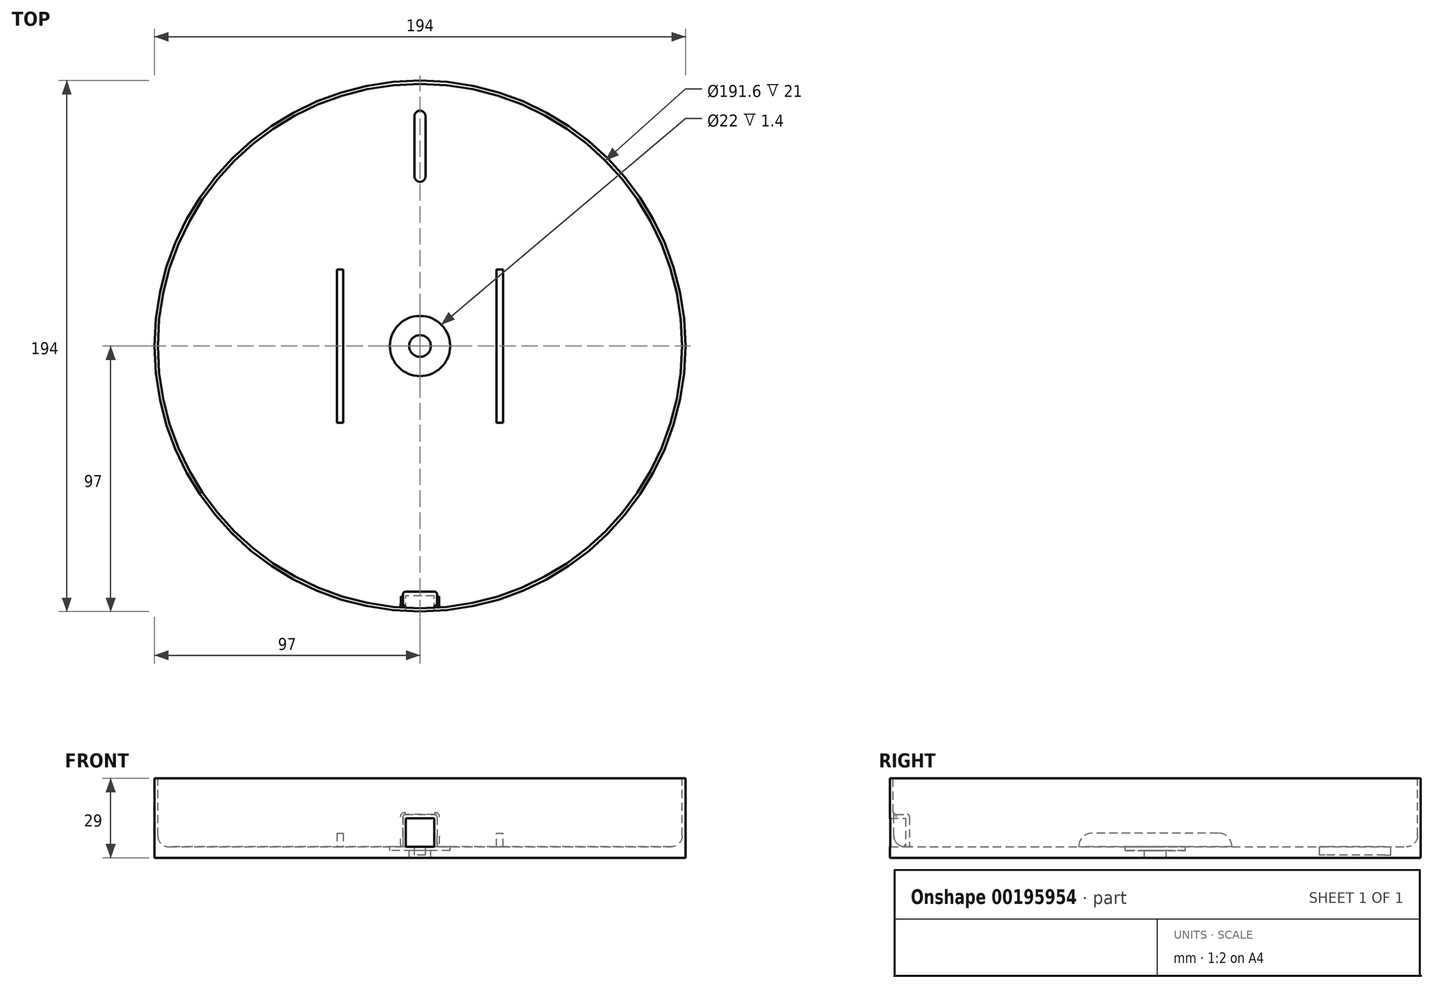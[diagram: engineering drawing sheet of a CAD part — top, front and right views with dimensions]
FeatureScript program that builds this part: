
annotation { "Feature Type Name" : "Feature", "Feature Type Description" : "" }
export const myFeature = defineFeature(function(context is Context, id is Id, definition is map)
    precondition{}
    {
        {
            var Q0;
            Q0=qCreatedBy(makeId("Top.planeOp"),FACE);
            var sketch = newSketch(context, id + "F0", { "sketchPlane" : qUnion([Q0])});
            skCircle(sketch, "E0", {"center": v(0, 0) * mm, "radius": 97 * mm});
            skSolve(sketch);
        }
        {
            var Q0;
            Q0 = qSketchRegion(id + "F0", true);
            extrude(context, id + "F1", {"entities" : qUnion([Q0]), "depth" : 29 * mm});
        }
        {
            var Q0;
            Q0=makeQuery(id+"F1.opExtrude","CAP_FACE",FACE,{"disambiguationData":[OSD([sQuery(id+"F0.wireOp",EDGE,"E0")])],"isStart":false});
            var sketch = newSketch(context, id + "F2", { "sketchPlane" : qUnion([Q0])});
            skCircle(sketch, "E1", {"center": v(0, 0) * mm, "radius": 95.8 * mm});
            skSolve(sketch);
        }
        {
            var Q0;
            Q0 = qSketchRegion(id + "F2", true);
            extrude(context, id + "F3", {"entities" : qUnion([Q0]), "operationType" : NewBodyOperationType.REMOVE, "oppositeDirection" : true, "depth" : 25 * mm});
        }
        {
            var Q0;
            Q0=makeQuery(id+"F3.boolean.opBoolean","COPY",FACE,{"derivedFrom":makeQuery(id+"F3.opExtrude","CAP_FACE",FACE,{"disambiguationData":[OSD([sQuery(id+"F2.wireOp",EDGE,"E1")])],"isStart":false})});
            var sketch = newSketch(context, id + "F4", { "sketchPlane" : qUnion([Q0])});
            skCircle(sketch, "E2", {"center": v(0, 0) * mm, "radius": 3.95 * mm});
            skSolve(sketch);
        }
        {
            var Q0;
            Q0 = qSketchRegion(id + "F4", true);
            extrude(context, id + "F5", {"entities" : qUnion([Q0]), "operationType" : NewBodyOperationType.REMOVE, "oppositeDirection" : true, "depth" : 25 * mm});
        }
        {
            var Q0;
            Q0=makeQuery(id+"F3.boolean.opBoolean","COPY",FACE,{"derivedFrom":makeQuery(id+"F3.opExtrude","CAP_FACE",FACE,{"disambiguationData":[OSD([sQuery(id+"F2.wireOp",EDGE,"E1")])],"isStart":false})});
            var sketch = newSketch(context, id + "F6", { "sketchPlane" : qUnion([Q0])});
            skCircle(sketch, "E3", {"center": v(0, 0) * mm, "radius": 11 * mm});
            skSolve(sketch);
        }
        {
            var Q0;
            Q0 = qSketchRegion(id + "F6", true);
            extrude(context, id + "F7", {"entities" : qUnion([Q0]), "operationType" : NewBodyOperationType.REMOVE, "oppositeDirection" : true, "depth" : 1.4 * mm});
        }
        {
            var Q0;
            Q0=makeQuery(id+"F3.boolean.opBoolean","COPY",FACE,{"derivedFrom":makeQuery(id+"F3.opExtrude","CAP_FACE",FACE,{"disambiguationData":[OSD([sQuery(id+"F2.wireOp",EDGE,"E1")])],"isStart":false})});
            var sketch = newSketch(context, id + "F8", { "sketchPlane" : qUnion([Q0])});
            skLineSegment(sketch, "E4.bottom", {"start": v(-30.4, 28) * mm, "end": v(30.4, 28) * mm});
            skLineSegment(sketch, "E4.top", {"start": v(-30.4, -28) * mm, "end": v(30.4, -28) * mm});
            skLineSegment(sketch, "E4.left", {"start": v(-30.4, 28) * mm, "end": v(-30.4, -28) * mm});
            skLineSegment(sketch, "E4.right", {"start": v(30.4, 28) * mm, "end": v(30.4, -28) * mm});
            skPoint(sketch, "E4.middle", {"position": v(0, 0) * mm});
            skLineSegment(sketch, "E5.bottom", {"start": v(-28, 28) * mm, "end": v(28, 28) * mm});
            skLineSegment(sketch, "E5.top", {"start": v(-28, -28) * mm, "end": v(28, -28) * mm});
            skLineSegment(sketch, "E5.left", {"start": v(-28, 28) * mm, "end": v(-28, -28) * mm});
            skLineSegment(sketch, "E5.right", {"start": v(28, 28) * mm, "end": v(28, -28) * mm});
            skSolve(sketch);
        }
        {
            var Q0;
            {var subQ2=sQuery(id+"F8.wireOp",EDGE,"E4.left");Q0=makeQuery(id+"F8.imprint","IMPRINT",FACE,{"disambiguationData":[TD([[makeQuery(id+"F8.imprint","IMPRINT",EDGE,{"derivedFrom":subQ2}),1.0]])]});}
            var Q1;
            {var subQ0=sQuery(id+"F8.wireOp",EDGE,"E4.right");Q1=makeQuery(id+"F8.imprint","IMPRINT",FACE,{"disambiguationData":[TD([[makeQuery(id+"F8.imprint","IMPRINT",EDGE,{"derivedFrom":subQ0}),-1.0]])]});}
            extrude(context, id + "F9", {"entities" : qUnion([Q0, Q1]), "operationType" : NewBodyOperationType.ADD, "depth" : 5 * mm});
        }
        {
            var Q0;
            {var subQ0=sQuery(id+"F8.wireOp",EDGE,"E4.bottom");Q0=makeQuery(id+"F9.opExtrude","CAP_EDGE",EDGE,{"disambiguationData":[OSD([subQ0]),TDD([makeQuery(id+"F8.imprint","IMPRINT",EDGE,{"disambiguationData":[TD([[makeQuery(id+"F8.imprint","INTERSECT",VERTEX,{"derivedFrom":[subQ0,sQuery(id+"F8.wireOp",EDGE,"E5.left")]}),1.0]])],"derivedFrom":subQ0})])],"isStart":false});}
            var Q1;
            {var subQ0=sQuery(id+"F8.wireOp",EDGE,"E4.top");Q1=makeQuery(id+"F9.opExtrude","CAP_EDGE",EDGE,{"disambiguationData":[OSD([subQ0]),TDD([makeQuery(id+"F8.imprint","IMPRINT",EDGE,{"disambiguationData":[TD([[makeQuery(id+"F8.imprint","INTERSECT",VERTEX,{"derivedFrom":[subQ0,sQuery(id+"F8.wireOp",EDGE,"E5.left")]}),1.0]])],"derivedFrom":subQ0})])],"isStart":false});}
            var Q2;
            {var subQ0=sQuery(id+"F8.wireOp",EDGE,"E4.top");Q2=makeQuery(id+"F9.opExtrude","CAP_EDGE",EDGE,{"disambiguationData":[OSD([subQ0]),TDD([makeQuery(id+"F8.imprint","IMPRINT",EDGE,{"disambiguationData":[TD([[makeQuery(id+"F8.imprint","INTERSECT",VERTEX,{"derivedFrom":[subQ0,sQuery(id+"F8.wireOp",EDGE,"E4.right")]}),1.0]])],"derivedFrom":subQ0})])],"isStart":false});}
            var Q3;
            {var subQ0=sQuery(id+"F8.wireOp",EDGE,"E4.bottom");Q3=makeQuery(id+"F9.opExtrude","CAP_EDGE",EDGE,{"disambiguationData":[OSD([subQ0]),TDD([makeQuery(id+"F8.imprint","IMPRINT",EDGE,{"disambiguationData":[TD([[makeQuery(id+"F8.imprint","INTERSECT",VERTEX,{"derivedFrom":[subQ0,sQuery(id+"F8.wireOp",EDGE,"E4.right")]}),1.0]])],"derivedFrom":subQ0})])],"isStart":false});}
            fillet(context, id + "F10", {"entities" : qUnion([Q0, Q1, Q2, Q3]), "radius" : 5 * mm, "tangentPropagation" : true, "allowEdgeOverflow" : false});
        }
        {
            var Q0;
            Q0=makeQuery(id+"F3.boolean.opBoolean","COPY",FACE,{"derivedFrom":makeQuery(id+"F3.opExtrude","CAP_FACE",FACE,{"disambiguationData":[OSD([sQuery(id+"F2.wireOp",EDGE,"E1")])],"isStart":false})});
            var sketch = newSketch(context, id + "F11", { "sketchPlane" : qUnion([Q0])});
            skLineSegment(sketch, "E6.bottom", {"start": v(6.2, -101.8) * mm, "end": v(-6.2, -101.8) * mm});
            skLineSegment(sketch, "E6.top", {"start": v(6.2, -89.8) * mm, "end": v(-6.2, -89.8) * mm});
            skLineSegment(sketch, "E6.left", {"start": v(6.2, -101.8) * mm, "end": v(6.2, -89.8) * mm});
            skLineSegment(sketch, "E6.right", {"start": v(-6.2, -101.8) * mm, "end": v(-6.2, -89.8) * mm});
            skPoint(sketch, "E6.middle", {"position": v(0, -95.8) * mm});
            skSolve(sketch);
        }
        {
            var Q0;
            {var subQ0=sQuery(id+"F11.wireOp",EDGE,"E6.top");Q0=makeQuery(id+"F11.imprint","IMPRINT",FACE,{"disambiguationData":[TD([[makeQuery(id+"F11.imprint","IMPRINT",EDGE,{"derivedFrom":subQ0}),1.0]])]});}
            extrude(context, id + "F12", {"entities" : qUnion([Q0]), "operationType" : NewBodyOperationType.ADD, "depth" : 11.8 * mm});
        }
        {
            var Q0;
            Q0=makeQuery(id+"F3.boolean.opBoolean","COPY",FACE,{"derivedFrom":makeQuery(id+"F3.opExtrude","CAP_FACE",FACE,{"disambiguationData":[OSD([sQuery(id+"F2.wireOp",EDGE,"E1")])],"isStart":false})});
            var sketch = newSketch(context, id + "F13", { "sketchPlane" : qUnion([Q0])});
            skLineSegment(sketch, "E7.bottom", {"start": v(5.2, -96.7) * mm, "end": v(-5.2, -96.7) * mm});
            skLineSegment(sketch, "E7.top", {"start": v(5.2, -91.3) * mm, "end": v(-5.2, -91.3) * mm});
            skLineSegment(sketch, "E7.left", {"start": v(5.2, -96.7) * mm, "end": v(5.2, -91.3) * mm});
            skLineSegment(sketch, "E7.right", {"start": v(-5.2, -96.7) * mm, "end": v(-5.2, -91.3) * mm});
            skPoint(sketch, "E7.middle", {"position": v(0, -94) * mm});
            skSolve(sketch);
        }
        {
            var Q0;
            Q0 = qSketchRegion(id + "F13", true);
            extrude(context, id + "F14", {"entities" : qUnion([Q0]), "operationType" : NewBodyOperationType.REMOVE, "depth" : 10.4 * mm});
        }
        {
            var Q0;
            Q0=makeQuery(id+"F14.boolean.opBoolean","COPY",FACE,{"derivedFrom":makeQuery(id+"F14.opExtrude","SWEPT_FACE",FACE,{"disambiguationData":[OSD([sQuery(id+"F13.wireOp",EDGE,"E7.bottom")])]})});
            extrude(context, id + "F15", {"entities" : qUnion([Q0]), "operationType" : NewBodyOperationType.REMOVE, "oppositeDirection" : true, "depth" : 25 * mm});
        }
        {
            var Q0;
            Q0=makeQuery(id+"F12.opExtrude","CAP_EDGE",EDGE,{"disambiguationData":[OSD([sQuery(id+"F11.wireOp",EDGE,"E6.right")])],"isStart":false});
            var Q1;
            Q1=makeQuery(id+"F12.opExtrude","CAP_EDGE",EDGE,{"disambiguationData":[OSD([sQuery(id+"F11.wireOp",EDGE,"E6.left")])],"isStart":false});
            var Q2;
            Q2=makeQuery(id+"F12.opExtrude","SWEPT_FACE",FACE,{"disambiguationData":[OSD([sQuery(id+"F11.wireOp",EDGE,"E6.top")])]});
            var Q3;
            Q3=makeQuery(id+"F12.opExtrude","SWEPT_FACE",FACE,{"disambiguationData":[OSD([sQuery(id+"F11.wireOp",EDGE,"E6.right")])]});
            var Q4;
            Q4=makeQuery(id+"F12.opExtrude","CAP_FACE",FACE,{"disambiguationData":[OSD([sQuery(id+"F2.wireOp",EDGE,"E1"),sQuery(id+"F11.wireOp",EDGE,"E6.top"),sQuery(id+"F11.wireOp",EDGE,"E6.left"),sQuery(id+"F11.wireOp",EDGE,"E6.right")])],"isStart":false});
            var Q5;
            Q5=makeQuery(id+"F12.opExtrude","SWEPT_FACE",FACE,{"disambiguationData":[OSD([sQuery(id+"F11.wireOp",EDGE,"E6.left")])]});
            fillet(context, id + "F16", {"entities" : qUnion([Q0, Q1, Q2, Q3, Q4, Q5]), "radius" : 0.8 * mm, "tangentPropagation" : true, "allowEdgeOverflow" : false});
        }
        {
            var Q0;
            Q0=makeQuery(id+"F3.boolean.opBoolean","COPY",EDGE,{"derivedFrom":makeQuery(id+"F3.opExtrude","CAP_EDGE",EDGE,{"disambiguationData":[OSD([sQuery(id+"F2.wireOp",EDGE,"E1")])],"isStart":false})});
            fillet(context, id + "F17", {"entities" : qUnion([Q0]), "radius" : 4 * mm, "tangentPropagation" : true, "allowEdgeOverflow" : false});
        }
        {
            var Q0;
            Q0=makeQuery(id+"F3.boolean.opBoolean","COPY",FACE,{"derivedFrom":makeQuery(id+"F3.opExtrude","CAP_FACE",FACE,{"disambiguationData":[OSD([sQuery(id+"F2.wireOp",EDGE,"E1")])],"isStart":false})});
            var sketch = newSketch(context, id + "F18", { "sketchPlane" : qUnion([Q0])});
            skLineSegment(sketch, "E8", {"start": v(0, 84) * mm, "end": v(0, 62) * mm});
            skArc(sketch, "E9.0.startCap", {"start": v(-2, 84) * mm, "mid": v(0, 86) * mm, "end": v(2, 84) * mm});
            skArc(sketch, "E9.0.endCap", {"start": v(2, 62) * mm, "mid": v(0, 60) * mm, "end": v(-2, 62) * mm});
            skLineSegment(sketch, "E9.0.left", {"start": v(2, 84) * mm, "end": v(2, 62) * mm});
            skLineSegment(sketch, "E9.0.right", {"start": v(-2, 84) * mm, "end": v(-2, 62) * mm});
            skSolve(sketch);
        }
        {
            var Q0;
            Q0 = qSketchRegion(id + "F18", true);
            extrude(context, id + "F19", {"entities" : qUnion([Q0]), "operationType" : NewBodyOperationType.REMOVE, "oppositeDirection" : true, "depth" : 3 * mm});
        }
    });
